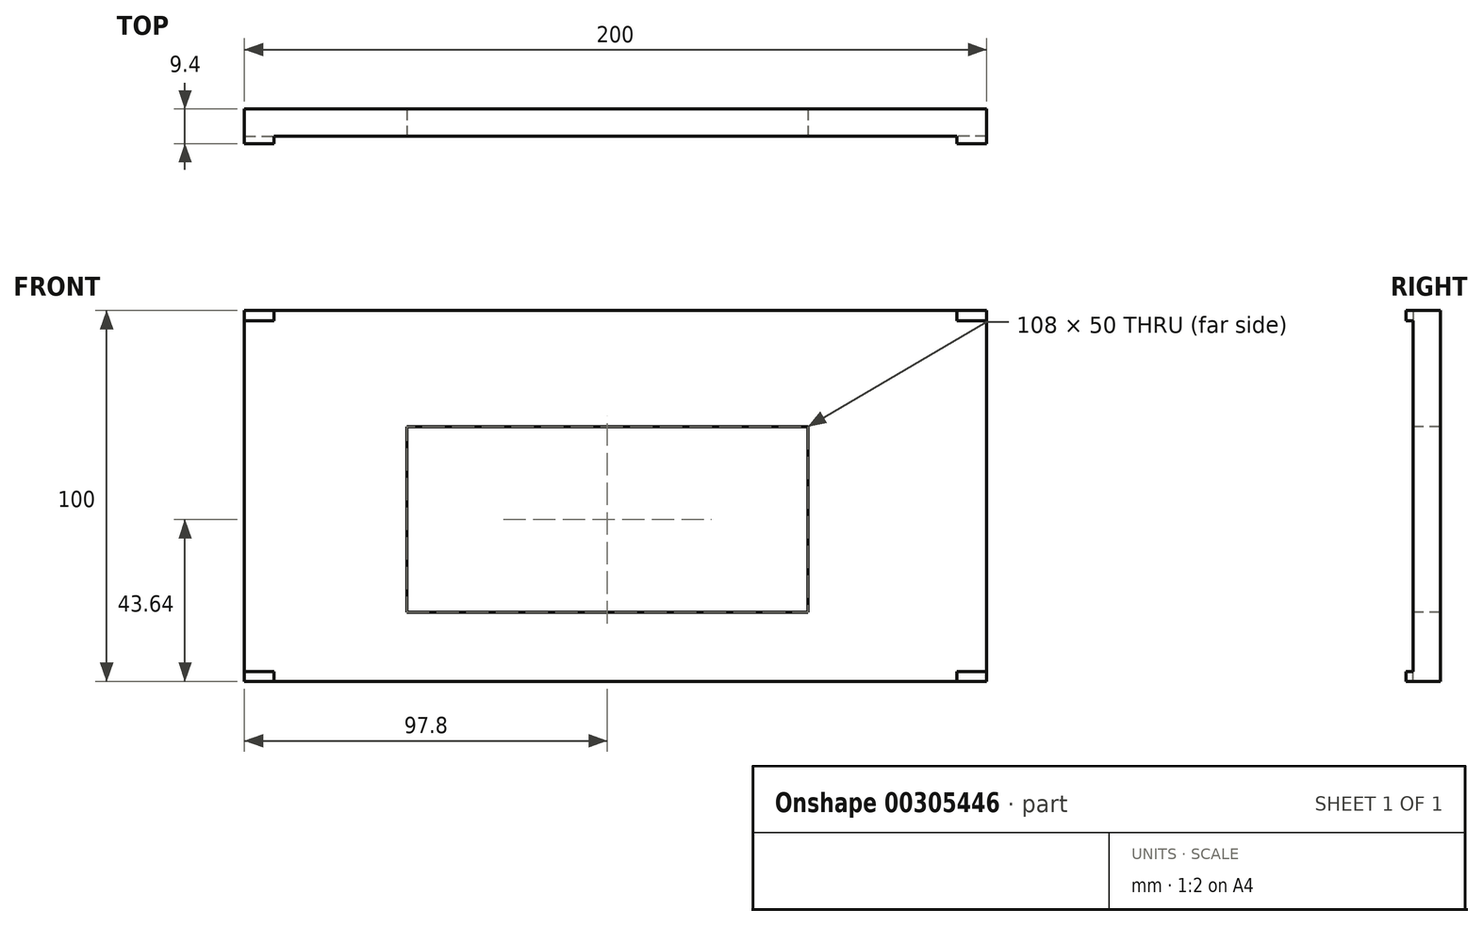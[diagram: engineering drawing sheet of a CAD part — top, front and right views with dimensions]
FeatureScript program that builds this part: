
annotation { "Feature Type Name" : "Feature", "Feature Type Description" : "" }
export const myFeature = defineFeature(function(context is Context, id is Id, definition is map)
    precondition{}
    {
        {
            var Q0;
            Q0=qCreatedBy(makeId("Front.planeOp"),FACE);
            var sketch = newSketch(context, id + "F0", { "sketchPlane" : qUnion([Q0])});
            skLineSegment(sketch, "E0.bottom", {"start": v(-97.8, 56.36) * mm, "end": v(102.2, 56.36) * mm});
            skLineSegment(sketch, "E0.top", {"start": v(-97.8, -43.64) * mm, "end": v(102.2, -43.64) * mm});
            skLineSegment(sketch, "E0.left", {"start": v(-97.8, 56.36) * mm, "end": v(-97.8, -43.64) * mm});
            skLineSegment(sketch, "E0.right", {"start": v(102.2, 56.36) * mm, "end": v(102.2, -43.64) * mm});
            skSolve(sketch);
        }
        {
            var Q0;
            Q0=makeQuery(id+"F0.imprint","IMPRINT",FACE,{"disambiguationData":[TD([[makeQuery(id+"F0.imprint","IMPRINT",EDGE,{"derivedFrom":sQuery(id+"F0.wireOp",EDGE,"E0.bottom")}),-1.0]])]});
            extrude(context, id + "F1", {"entities" : qUnion([Q0]), "depth" : 7.4 * mm});
        }
        {
            var Q0;
            Q0=makeQuery(id+"F1.opExtrude","CAP_FACE",FACE,{"disambiguationData":[OSD([sQuery(id+"F0.wireOp",EDGE,"E0.bottom"),sQuery(id+"F0.wireOp",EDGE,"E0.top"),sQuery(id+"F0.wireOp",EDGE,"E0.left"),sQuery(id+"F0.wireOp",EDGE,"E0.right")])],"isStart":false});
            var sketch = newSketch(context, id + "F2", { "sketchPlane" : qUnion([Q0])});
            skLineSegment(sketch, "E1.bottom", {"start": v(-97.8, 56.36) * mm, "end": v(-89.8, 56.36) * mm});
            skLineSegment(sketch, "E1.top", {"start": v(-97.8, 53.66) * mm, "end": v(-89.8, 53.66) * mm});
            skLineSegment(sketch, "E1.left", {"start": v(-97.8, 56.36) * mm, "end": v(-97.8, 53.66) * mm});
            skLineSegment(sketch, "E1.right", {"start": v(-89.8, 56.36) * mm, "end": v(-89.8, 53.66) * mm});
            skLineSegment(sketch, "E2.bottom", {"start": v(102.2, 56.36) * mm, "end": v(94.2, 56.36) * mm});
            skLineSegment(sketch, "E2.top", {"start": v(102.2, 53.66) * mm, "end": v(94.2, 53.66) * mm});
            skLineSegment(sketch, "E2.left", {"start": v(102.2, 56.36) * mm, "end": v(102.2, 53.66) * mm});
            skLineSegment(sketch, "E2.right", {"start": v(94.2, 56.36) * mm, "end": v(94.2, 53.66) * mm});
            skLineSegment(sketch, "E3.bottom", {"start": v(-97.8, -43.64) * mm, "end": v(-89.8, -43.64) * mm});
            skLineSegment(sketch, "E3.top", {"start": v(-97.8, -40.94) * mm, "end": v(-89.8, -40.94) * mm});
            skLineSegment(sketch, "E3.left", {"start": v(-97.8, -43.64) * mm, "end": v(-97.8, -40.94) * mm});
            skLineSegment(sketch, "E3.right", {"start": v(-89.8, -43.64) * mm, "end": v(-89.8, -40.94) * mm});
            skLineSegment(sketch, "E4.bottom", {"start": v(102.2, -43.64) * mm, "end": v(94.2, -43.64) * mm});
            skLineSegment(sketch, "E4.top", {"start": v(102.2, -40.94) * mm, "end": v(94.2, -40.94) * mm});
            skLineSegment(sketch, "E4.left", {"start": v(102.2, -43.64) * mm, "end": v(102.2, -40.94) * mm});
            skLineSegment(sketch, "E4.right", {"start": v(94.2, -43.64) * mm, "end": v(94.2, -40.94) * mm});
            skSolve(sketch);
        }
        {
            var Q0;
            Q0=makeQuery(id+"F2.imprint","IMPRINT",FACE,{"disambiguationData":[TD([[makeQuery(id+"F2.imprint","IMPRINT",EDGE,{"derivedFrom":sQuery(id+"F2.wireOp",EDGE,"E1.bottom")}),-1.0]])]});
            var Q1;
            Q1=makeQuery(id+"F2.imprint","IMPRINT",FACE,{"disambiguationData":[TD([[makeQuery(id+"F2.imprint","IMPRINT",EDGE,{"derivedFrom":sQuery(id+"F2.wireOp",EDGE,"E2.bottom")}),-1.0]])]});
            var Q2;
            Q2=makeQuery(id+"F2.imprint","IMPRINT",FACE,{"disambiguationData":[TD([[makeQuery(id+"F2.imprint","IMPRINT",EDGE,{"derivedFrom":sQuery(id+"F2.wireOp",EDGE,"E4.bottom")}),1.0]])]});
            var Q3;
            Q3=makeQuery(id+"F2.imprint","IMPRINT",FACE,{"disambiguationData":[TD([[makeQuery(id+"F2.imprint","IMPRINT",EDGE,{"derivedFrom":sQuery(id+"F2.wireOp",EDGE,"E3.bottom")}),1.0]])]});
            extrude(context, id + "F3", {"entities" : qUnion([Q0, Q1, Q2, Q3]), "operationType" : NewBodyOperationType.ADD, "depth" : 2 * mm});
        }
        {
            var Q0;
            Q0=makeQuery(id+"F1.opExtrude","CAP_FACE",FACE,{"disambiguationData":[OSD([sQuery(id+"F0.wireOp",EDGE,"E0.bottom"),sQuery(id+"F0.wireOp",EDGE,"E0.top"),sQuery(id+"F0.wireOp",EDGE,"E0.left"),sQuery(id+"F0.wireOp",EDGE,"E0.right")])],"isStart":false});
            var sketch = newSketch(context, id + "F4", { "sketchPlane" : qUnion([Q0])});
            skLineSegment(sketch, "E5.bottom", {"start": v(-54, 25) * mm, "end": v(54, 25) * mm});
            skLineSegment(sketch, "E5.top", {"start": v(-54, -25) * mm, "end": v(54, -25) * mm});
            skLineSegment(sketch, "E5.left", {"start": v(-54, 25) * mm, "end": v(-54, -25) * mm});
            skLineSegment(sketch, "E5.right", {"start": v(54, 25) * mm, "end": v(54, -25) * mm});
            skPoint(sketch, "E5.middle", {"position": v(0, 0) * mm});
            skSolve(sketch);
        }
        {
            var Q0;
            Q0=makeQuery(id+"F4.imprint","IMPRINT",FACE,{"disambiguationData":[TD([[makeQuery(id+"F4.imprint","IMPRINT",EDGE,{"derivedFrom":sQuery(id+"F4.wireOp",EDGE,"E5.bottom")}),-1.0]])]});
            extrude(context, id + "F5", {"entities" : qUnion([Q0]), "operationType" : NewBodyOperationType.REMOVE, "endBound" : BoundingType.THROUGH_ALL, "oppositeDirection" : true, "depth" : 25 * mm});
        }
    });
